# Revit family: SoapDispenser_Metlam_Recessed_Vertical
name_source: partatom
category: Generic Models
revit_build: Autodesk Revit Architecture 2013 (Build: 20120221_2030(x64)
units: mm (PartAtom-declared; Revit-internal decimal feet)

## types (1)
- Metlam WM Vertical Standard
    Assembly Code = E1090900
    Depth = 159 mm  [stored 0.521654 ft]
    Description = Recessed Vertical Liquid Soap Dispenser Stainless Steel
    FilterObject_ANZRS = Soap Dispenser
    Height = 260 mm  [stored 0.853018 ft]
    Keywords = CAPACITY 1.2L with lockable hinged lid (key provided)
    Manufacturer = Metlam
    Material Glass = Glass
    Material Main = Stainless Steel, Satin
    Material Nozzle = Stainless Steel, Polished
    Model = Recessed Vertical
    ModifiedIssue_ANZRS = 130318.01 $
    Nozzle Standard = Yes
    Product Code = ML 641 AS
    StyleOrType_ANZRS = Sanitary Ware
    URL = http://www.metlam.com.au
    Width = 150 mm  [stored 0.492126 ft]

note: [stored X ft] marks values corroborated as IEEE doubles in the binary element streams (Revit-internal decimal feet)

## geometry (parser evidence)
native form markers: Blend x13, Sweep x1
no freeform markers — native parametric forms only
